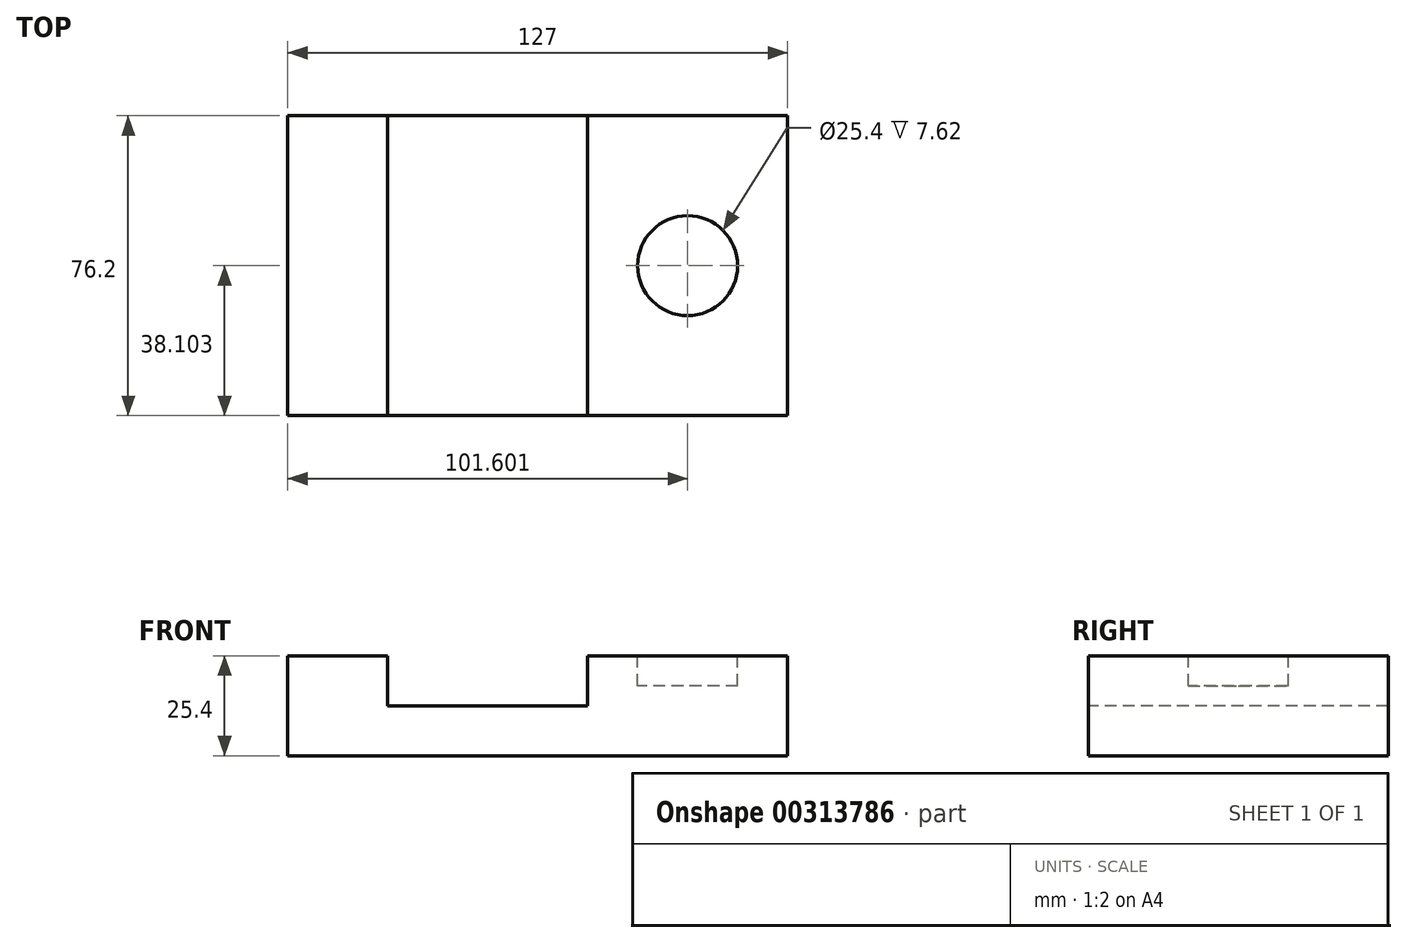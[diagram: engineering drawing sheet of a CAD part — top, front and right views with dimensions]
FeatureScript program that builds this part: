
annotation { "Feature Type Name" : "Feature", "Feature Type Description" : "" }
export const myFeature = defineFeature(function(context is Context, id is Id, definition is map)
    precondition{}
    {
        {
            var Q0;
            Q0=qCreatedBy(makeId("Top.planeOp"),FACE);
            var sketch = newSketch(context, id + "F0", { "sketchPlane" : qUnion([Q0])});
            skLineSegment(sketch, "E0.bottom", {"start": v(-59.04, 47.86) * mm, "end": v(67.96, 47.86) * mm});
            skLineSegment(sketch, "E0.top", {"start": v(-59.04, -28.34) * mm, "end": v(67.96, -28.34) * mm});
            skLineSegment(sketch, "E0.left", {"start": v(-59.04, 47.86) * mm, "end": v(-59.04, -28.34) * mm});
            skLineSegment(sketch, "E0.right", {"start": v(67.96, 47.86) * mm, "end": v(67.96, -28.34) * mm});
            skSolve(sketch);
        }
        {
            var Q0;
            Q0=makeQuery(id+"F0.imprint","IMPRINT",FACE,{"disambiguationData":[TD([[makeQuery(id+"F0.imprint","IMPRINT",EDGE,{"derivedFrom":sQuery(id+"F0.wireOp",EDGE,"E0.bottom")}),-1.0]])]});
            extrude(context, id + "F1", {"entities" : qUnion([Q0]), "depth" : 25.4 * mm});
        }
        {
            var Q0;
            Q0=makeQuery(id+"F1.opExtrude","CAP_FACE",FACE,{"disambiguationData":[OSD([sQuery(id+"F0.wireOp",EDGE,"E0.bottom"),sQuery(id+"F0.wireOp",EDGE,"E0.top"),sQuery(id+"F0.wireOp",EDGE,"E0.left"),sQuery(id+"F0.wireOp",EDGE,"E0.right")])],"isStart":false});
            var sketch = newSketch(context, id + "F2", { "sketchPlane" : qUnion([Q0])});
            skLineSegment(sketch, "E1.bottom", {"start": v(-59.04, 47.86) * mm, "end": v(-33.64, 47.86) * mm});
            skLineSegment(sketch, "E1.top", {"start": v(-59.04, -28.34) * mm, "end": v(-33.64, -28.34) * mm});
            skLineSegment(sketch, "E1.left", {"start": v(-59.04, 47.86) * mm, "end": v(-59.04, -28.34) * mm});
            skLineSegment(sketch, "E1.right", {"start": v(-33.64, 47.86) * mm, "end": v(-33.64, -28.34) * mm});
            skLineSegment(sketch, "E2.bottom", {"start": v(17.16, 47.86) * mm, "end": v(-33.64, 47.86) * mm});
            skLineSegment(sketch, "E2.top", {"start": v(17.16, -28.34) * mm, "end": v(-33.64, -28.34) * mm});
            skLineSegment(sketch, "E2.left", {"start": v(17.16, 47.86) * mm, "end": v(17.16, -28.34) * mm});
            skLineSegment(sketch, "E3.bottom", {"start": v(17.16, 47.86) * mm, "end": v(67.96, 47.86) * mm});
            skLineSegment(sketch, "E3.top", {"start": v(17.16, -28.34) * mm, "end": v(67.96, -28.34) * mm});
            skLineSegment(sketch, "E3.right", {"start": v(67.96, 47.86) * mm, "end": v(67.96, -28.34) * mm});
            skSolve(sketch);
        }
        {
            var Q0;
            Q0=makeQuery(id+"F2.imprint","IMPRINT",FACE,{"disambiguationData":[TD([[makeQuery(id+"F2.imprint","IMPRINT",EDGE,{"derivedFrom":sQuery(id+"F2.wireOp",EDGE,"E2.bottom")}),-1.0]])]});
            extrude(context, id + "F3", {"entities" : qUnion([Q0]), "operationType" : NewBodyOperationType.REMOVE, "oppositeDirection" : true, "depth" : 12.7 * mm});
        }
        {
            var Q0;
            {var subQ0=sQuery(id+"F0.wireOp",EDGE,"E0.bottom");var subQ1=sQuery(id+"F0.wireOp",EDGE,"E0.right");var subQ2=sQuery(id+"F0.wireOp",EDGE,"E0.top");Q0=makeQuery(id+"F3.boolean.opBoolean","SPLIT",FACE,{"disambiguationData":[TD([makeQuery(id+"F1.opExtrude","SWEPT_FACE",FACE,{"disambiguationData":[OSD([subQ1])]})])],"derivedFrom":makeQuery(id+"F1.opExtrude","CAP_FACE",FACE,{"disambiguationData":[OSD([subQ0,subQ2,sQuery(id+"F0.wireOp",EDGE,"E0.left"),subQ1])],"isStart":false})});}
            var sketch = newSketch(context, id + "F4", { "sketchPlane" : qUnion([Q0])});
            skCircle(sketch, "E4", {"center": v(42.56, 9.76) * mm, "radius": 12.7 * mm});
            skPoint(sketch, "E4.centerSnap0", {"position": v(17.16, 9.76) * mm});
            skSolve(sketch);
        }
        {
            var Q0;
            Q0=makeQuery(id+"F4.imprint","IMPRINT",FACE,{"disambiguationData":[TD([[makeQuery(id+"F4.imprint","IMPRINT",EDGE,{"derivedFrom":sQuery(id+"F4.wireOp",EDGE,"E4")}),1.0]])]});
            extrude(context, id + "F5", {"entities" : qUnion([Q0]), "operationType" : NewBodyOperationType.REMOVE, "oppositeDirection" : true, "depth" : 7.62 * mm});
        }
    });
